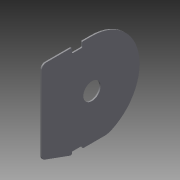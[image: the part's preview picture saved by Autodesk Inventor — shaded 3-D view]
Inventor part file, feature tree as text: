
AUTODESK INVENTOR PART (.ipt)
format: ipt  version: 2015 (Build 190159000, 159)  size: 130,560 bytes
history: native  units: mm
features: fillet x2, extrude x1, sketch x1
ambient origin geometry x8: Origin, YZ Plane, XZ Plane, XY Plane, X Axis, Y Axis, Z Axis, Center Point
bodies: Body1 (feature_tree)
feature tree (4):
  extrude  "Extrusion4"  Depth=1.5mm
  fillet  "Fillet1"  Radius=20.0mm
  fillet  "Fillet2"  Radius=52.0mm
  sketch  "Sketch1"  dims[d4=94.0mm d8=60.0mm d9=20.0mm d13=52.0mm d18=55.0mm d20=100.0mm d31=55.0mm d34=58.0mm d52=5.0mm d54=47.0mm d56=1.0mm d59=20.0mm d60=12.0mm d61=6.0mm d64=3.0mm d65=0.5mm d69=1.5mm d70=0.0mm d71=95.0mm d72=5.0mm d74=19.198622mm d75=12.0mm d76=3.0mm d77=1.5mm]
